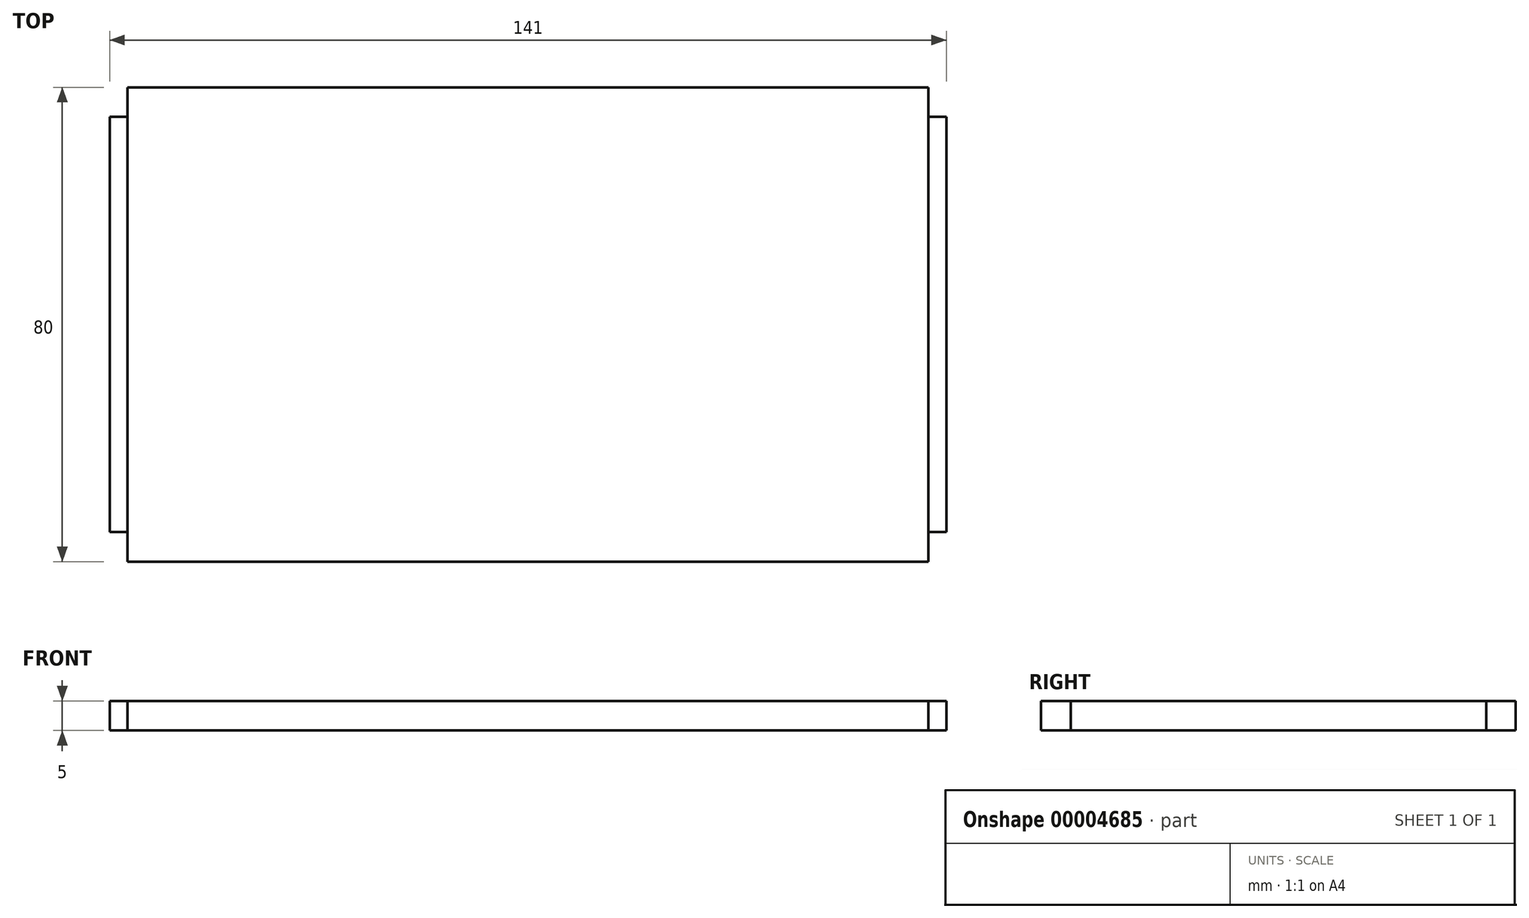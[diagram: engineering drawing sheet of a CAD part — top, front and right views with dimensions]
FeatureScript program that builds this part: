
annotation { "Feature Type Name" : "Feature", "Feature Type Description" : "" }
export const myFeature = defineFeature(function(context is Context, id is Id, definition is map)
    precondition{}
    {
        {
            var Q0;
            Q0=qCreatedBy(makeId("Top.planeOp"),FACE);
            var sketch = newSketch(context, id + "F0", { "sketchPlane" : qUnion([Q0])});
            skLineSegment(sketch, "E0.rect.bottom", {"start": v(67.5, 40) * mm, "end": v(-67.5, 40) * mm});
            skLineSegment(sketch, "E0.rect.top", {"start": v(67.5, -40) * mm, "end": v(-67.5, -40) * mm});
            skLineSegment(sketch, "E0.rect.left", {"start": v(67.5, 40) * mm, "end": v(67.5, -40) * mm});
            skLineSegment(sketch, "E0.rect.right", {"start": v(-67.5, 40) * mm, "end": v(-67.5, -40) * mm});
            skPoint(sketch, "E0.rect.middle", {"position": v(0, 0) * mm});
            skSolve(sketch);
        }
        {
            var Q0;
            Q0 = qSketchRegion(id + "F0", true);
            extrude(context, id + "F1", {"entities" : qUnion([Q0]), "depth" : 5 * mm});
        }
        {
            var Q0;
            Q0=makeQuery(id+"F1.opExtrude","SWEPT_FACE",FACE,{"disambiguationData":[OSD([sQuery(id+"F0.wireOp",EDGE,"E0.rect.right")])]});
            var sketch = newSketch(context, id + "F2", { "sketchPlane" : qUnion([Q0])});
            skLineSegment(sketch, "E1.rect.bottom", {"start": v(35, 5) * mm, "end": v(-35, 5) * mm});
            skLineSegment(sketch, "E1.rect.top", {"start": v(35, 0) * mm, "end": v(-35, 0) * mm});
            skLineSegment(sketch, "E1.rect.left", {"start": v(35, 5) * mm, "end": v(35, 0) * mm});
            skLineSegment(sketch, "E1.rect.right", {"start": v(-35, 5) * mm, "end": v(-35, 0) * mm});
            skPoint(sketch, "E1.rect.middle", {"position": v(0, 2.5) * mm});
            skSolve(sketch);
        }
        {
            var Q0;
            Q0 = qSketchRegion(id + "F2", true);
            extrude(context, id + "F3", {"entities" : qUnion([Q0]), "operationType" : NewBodyOperationType.ADD, "depth" : 3 * mm});
        }
        {
            var Q0;
            Q0=makeQuery(id+"F1.opExtrude","SWEPT_BODY",BODY,{"disambiguationData":[OSD([sQuery(id+"F0.wireOp",EDGE,"E0.rect.bottom"),sQuery(id+"F0.wireOp",EDGE,"E0.rect.top"),sQuery(id+"F0.wireOp",EDGE,"E0.rect.left"),sQuery(id+"F0.wireOp",EDGE,"E0.rect.right")])]});
            var Q1;
            Q1=qCreatedBy(makeId("Right.planeOp"),FACE);
            mirror(context, id + "F4", {"entities" : qUnion([Q0]), "mirrorPlane" : qUnion([Q1])});
        }
    });
